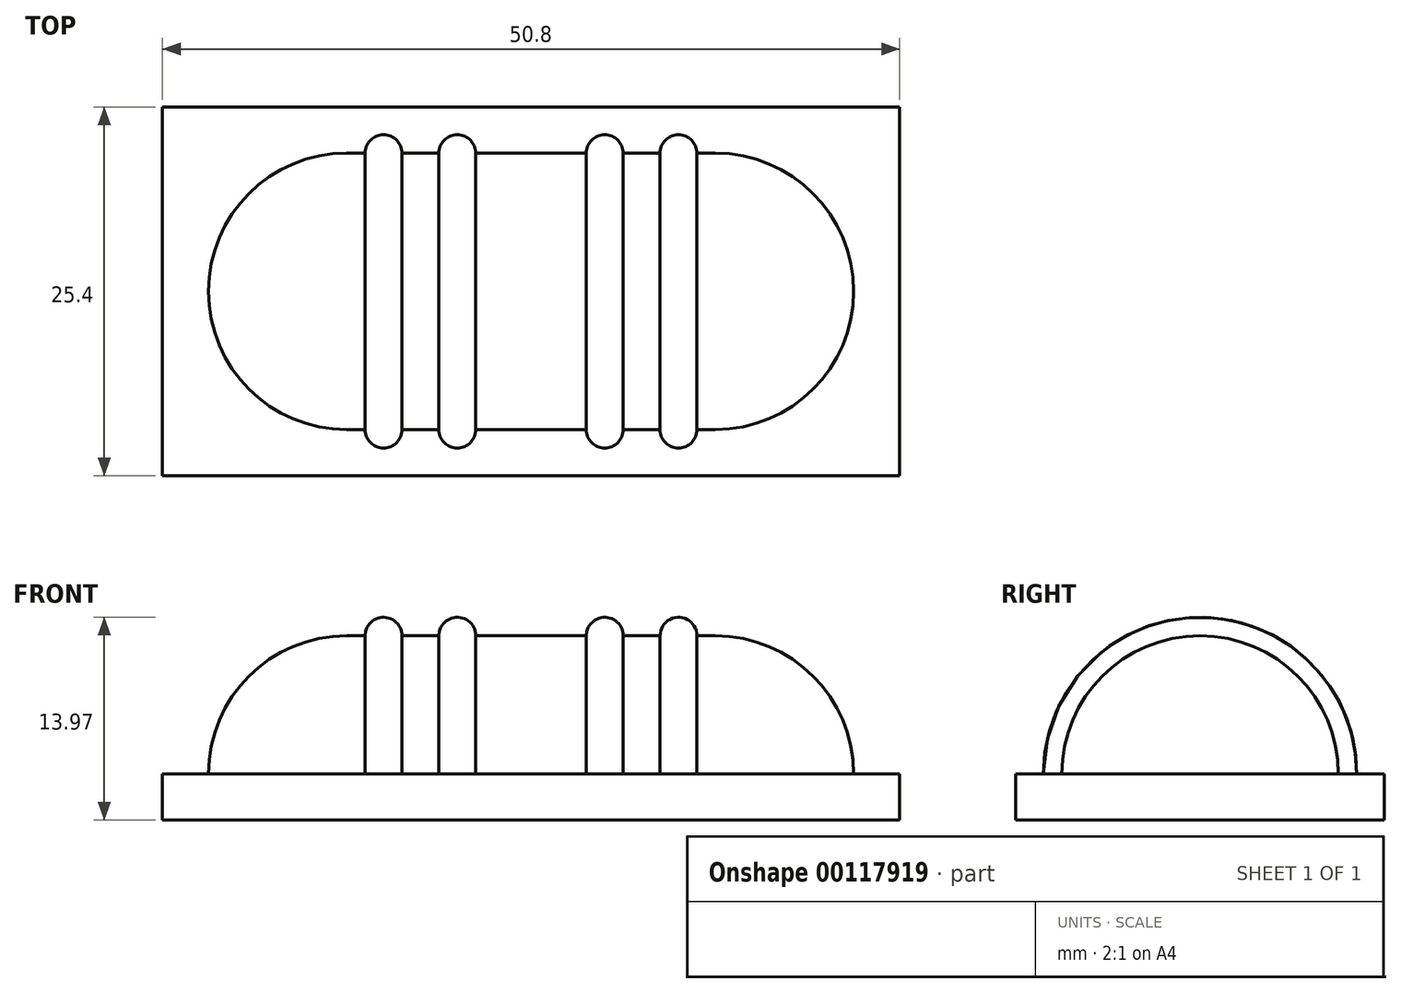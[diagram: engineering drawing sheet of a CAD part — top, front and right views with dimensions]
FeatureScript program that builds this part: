
annotation { "Feature Type Name" : "Feature", "Feature Type Description" : "" }
export const myFeature = defineFeature(function(context is Context, id is Id, definition is map)
    precondition{}
    {
        {
            var Q0;
            Q0=qCreatedBy(makeId("Top.planeOp"),FACE);
            var sketch = newSketch(context, id + "F0", { "sketchPlane" : qUnion([Q0])});
            skLineSegment(sketch, "E0.bottom", {"start": v(0, 0) * mm, "end": v(50.8, 0) * mm});
            skLineSegment(sketch, "E0.top", {"start": v(0, 25.4) * mm, "end": v(50.8, 25.4) * mm});
            skLineSegment(sketch, "E0.left", {"start": v(0, 0) * mm, "end": v(0, 25.4) * mm});
            skLineSegment(sketch, "E0.right", {"start": v(50.8, 0) * mm, "end": v(50.8, 25.4) * mm});
            skLineSegment(sketch, "E1", {"start": v(25.4, 25.4) * mm, "end": v(25.4, 0) * mm, "construction": true});
            skLineSegment(sketch, "E2.bottom", {"start": v(12.7, 22.22) * mm, "end": v(38.1, 22.22) * mm});
            skLineSegment(sketch, "E2.top", {"start": v(12.7, 3.18) * mm, "end": v(38.1, 3.18) * mm});
            skLineSegment(sketch, "E2.left", {"start": v(12.7, 22.22) * mm, "end": v(12.7, 3.18) * mm});
            skLineSegment(sketch, "E2.right", {"start": v(38.1, 22.22) * mm, "end": v(38.1, 3.18) * mm});
            skSolve(sketch);
        }
        {
            var Q0;
            Q0 = qSketchRegion(id + "F0", true);
            var Q1;
            Q1=makeQuery(id+"F0.imprint","IMPRINT",FACE,{"disambiguationData":[TD([[makeQuery(id+"F0.imprint","IMPRINT",EDGE,{"derivedFrom":sQuery(id+"F0.wireOp",EDGE,"E2.bottom")}),-1.0]])]});
            extrude(context, id + "F1", {"entities" : qUnion([Q0, Q1]), "depth" : 3.17 * mm});
        }
        {
            var Q0;
            Q0=makeQuery(id+"F1.opExtrude","CAP_FACE",FACE,{"disambiguationData":[OSD([sQuery(id+"F0.wireOp",EDGE,"E0.bottom"),sQuery(id+"F0.wireOp",EDGE,"E0.top"),sQuery(id+"F0.wireOp",EDGE,"E0.left"),sQuery(id+"F0.wireOp",EDGE,"E0.right")])],"isStart":false});
            var sketch = newSketch(context, id + "F2", { "sketchPlane" : qUnion([Q0])});
            skLineSegment(sketch, "E3.0", {"start": v(12.7, 22.22) * mm, "end": v(38.1, 22.22) * mm});
            skLineSegment(sketch, "E3.1", {"start": v(12.7, 22.22) * mm, "end": v(12.7, 3.18) * mm});
            skLineSegment(sketch, "E3.2", {"start": v(12.7, 3.18) * mm, "end": v(38.1, 3.18) * mm});
            skLineSegment(sketch, "E3.3", {"start": v(38.1, 22.22) * mm, "end": v(38.1, 3.18) * mm});
            skLineSegment(sketch, "E3.4", {"start": v(25.4, 25.4) * mm, "end": v(25.4, 0) * mm});
            skLineSegment(sketch, "E4", {"start": v(0, 12.7) * mm, "end": v(50.8, 12.7) * mm});
            skSolve(sketch);
        }
        {
            var Q0;
            {var subQ5=sQuery(id+"F2.wireOp",EDGE,"E3.3");Q0=makeQuery(id+"F2.imprint","IMPRINT",FACE,{"disambiguationData":[TD([[makeQuery(id+"F2.imprint","IMPRINT",EDGE,{"derivedFrom":subQ5}),1.0]])]});}
            var sketch = newSketch(context, id + "F3", { "sketchPlane" : qUnion([Q0])});
            skLineSegment(sketch, "E5.0", {"start": v(38.1, 22.22) * mm, "end": v(38.1, 3.18) * mm});
            skArc(sketch, "E6", {"start": v(38.1, 22.22) * mm, "mid": v(47.62, 12.7) * mm, "end": v(38.1, 3.18) * mm});
            skLineSegment(sketch, "E7.0", {"start": v(12.7, 22.22) * mm, "end": v(12.7, 3.18) * mm});
            skArc(sketch, "E8", {"start": v(12.7, 22.22) * mm, "mid": v(3.18, 12.7) * mm, "end": v(12.7, 3.18) * mm});
            skSolve(sketch);
        }
        {
            var Q0;
            {var subQ0=sQuery(id+"F2.wireOp",EDGE,"E3.2");var subQ1=sQuery(id+"F2.wireOp",EDGE,"E3.1");var subQ2=makeQuery(id+"F2.imprint","INTERSECT",VERTEX,{"derivedFrom":[subQ1,subQ0]});Q0=makeQuery(id+"F2.imprint","IMPRINT",FACE,{"disambiguationData":[TD([[makeQuery(id+"F2.imprint","IMPRINT",EDGE,{"disambiguationData":[TD([[subQ2,1.0]])],"derivedFrom":subQ1}),1.0]])]});}
            var Q1;
            {var subQ0=sQuery(id+"F2.wireOp",EDGE,"E3.3");var subQ1=sQuery(id+"F2.wireOp",EDGE,"E3.2");var subQ2=makeQuery(id+"F2.imprint","INTERSECT",VERTEX,{"derivedFrom":[subQ1,subQ0]});Q1=makeQuery(id+"F2.imprint","IMPRINT",FACE,{"disambiguationData":[TD([[makeQuery(id+"F2.imprint","IMPRINT",EDGE,{"disambiguationData":[TD([[subQ2,1.0]])],"derivedFrom":subQ1}),1.0]])]});}
            var Q2;
            Q2=sQuery(id+"F2.wireOp",EDGE,"E4");
            revolve(context, id + "F4", {"operationType" : NewBodyOperationType.ADD, "entities" : qUnion([Q0, Q1]), "axis" : qUnion([Q2]), "revolveType" : RevolveType.ONE_DIRECTION, "oppositeDirection" : true, "angle" : 180 * degree});
        }
        {
            var Q0;
            Q0=qCreatedBy(makeId("Front.planeOp"),FACE);
            var sketch = newSketch(context, id + "F5", { "sketchPlane" : qUnion([Q0])});
            skLineSegment(sketch, "E9.0", {"start": v(12.7, 12.7) * mm, "end": v(12.7, 3.17) * mm});
            skLineSegment(sketch, "E9.1", {"start": v(3.18, 3.18) * mm, "end": v(12.7, 3.18) * mm});
            skLineSegment(sketch, "E9.2", {"start": v(38.1, 12.7) * mm, "end": v(38.1, 3.18) * mm});
            skLineSegment(sketch, "E9.3", {"start": v(47.62, 3.18) * mm, "end": v(38.1, 3.18) * mm});
            skArc(sketch, "E10", {"start": v(12.7, 12.7) * mm, "mid": v(5.96, 9.91) * mm, "end": v(3.18, 3.18) * mm});
            skArc(sketch, "E11", {"start": v(38.1, 12.7) * mm, "mid": v(44.84, 9.91) * mm, "end": v(47.62, 3.18) * mm});
            skSolve(sketch);
        }
        {
            var Q0;
            {var subQ1=sQuery(id+"F3.wireOp",EDGE,"E5.0");var subQ5=sQuery(id+"F2.wireOp",EDGE,"E4");var subQ6=makeQuery(id+"F2.imprint","IMPRINT",EDGE,{"disambiguationData":[TD([[makeQuery(id+"F2.imprint","INTERSECT",VERTEX,{"derivedFrom":[makeQuery(id+"F1.opExtrude","CAP_EDGE",EDGE,{"disambiguationData":[OSD([sQuery(id+"F0.wireOp",EDGE,"E0.right")])],"isStart":false}),subQ5]}),1.0]])],"derivedFrom":subQ5});var subQ7=makeQuery(id+"F3.imprint","INTERSECT",VERTEX,{"derivedFrom":[subQ6,subQ1]});Q0=makeQuery(id+"F3.imprint","IMPRINT",FACE,{"disambiguationData":[TD([[makeQuery(id+"F3.imprint","IMPRINT",EDGE,{"disambiguationData":[TD([[subQ7,-1.0]])],"derivedFrom":subQ1}),1.0]])]});}
            var Q1;
            {var subQ1=sQuery(id+"F3.wireOp",EDGE,"E5.0");var subQ5=sQuery(id+"F2.wireOp",EDGE,"E4");var subQ6=makeQuery(id+"F2.imprint","IMPRINT",EDGE,{"disambiguationData":[TD([[makeQuery(id+"F2.imprint","INTERSECT",VERTEX,{"derivedFrom":[makeQuery(id+"F1.opExtrude","CAP_EDGE",EDGE,{"disambiguationData":[OSD([sQuery(id+"F0.wireOp",EDGE,"E0.right")])],"isStart":false}),subQ5]}),1.0]])],"derivedFrom":subQ5});var subQ7=makeQuery(id+"F3.imprint","INTERSECT",VERTEX,{"derivedFrom":[subQ6,subQ1]});Q1=makeQuery(id+"F3.imprint","IMPRINT",FACE,{"disambiguationData":[TD([[makeQuery(id+"F3.imprint","IMPRINT",EDGE,{"disambiguationData":[TD([[subQ7,1.0]])],"derivedFrom":subQ1}),1.0]])]});}
            var Q2;
            Q2=sQuery(id+"F5.wireOp",EDGE,"E11");
            sweep(context, id + "F6", {"operationType" : NewBodyOperationType.ADD, "profiles" : qUnion([Q0, Q1]), "path" : qUnion([Q2])});
        }
        {
            var Q0;
            Q0=makeQuery(id+"F3.imprint","IMPRINT",FACE,{"disambiguationData":[TD([[makeQuery(id+"F3.imprint","IMPRINT",EDGE,{"derivedFrom":sQuery(id+"F3.wireOp",EDGE,"E7.0")}),-1.0]])]});
            var Q1;
            Q1=sQuery(id+"F5.wireOp",EDGE,"E10");
            sweep(context, id + "F7", {"operationType" : NewBodyOperationType.ADD, "profiles" : qUnion([Q0]), "path" : qUnion([Q1])});
        }
        {
            var Q0;
            Q0=makeQuery(id+"F1.opExtrude","CAP_FACE",FACE,{"disambiguationData":[OSD([sQuery(id+"F0.wireOp",EDGE,"E0.bottom"),sQuery(id+"F0.wireOp",EDGE,"E0.top"),sQuery(id+"F0.wireOp",EDGE,"E0.left"),sQuery(id+"F0.wireOp",EDGE,"E0.right")])],"isStart":false});
            var sketch = newSketch(context, id + "F8", { "sketchPlane" : qUnion([Q0])});
            skLineSegment(sketch, "E12.0", {"start": v(25.4, 25.4) * mm, "end": v(25.4, 0) * mm, "construction": true});
            skLineSegment(sketch, "E13.0", {"start": v(12.7, 22.22) * mm, "end": v(38.1, 22.22) * mm});
            skLineSegment(sketch, "E13.1", {"start": v(12.7, 22.22) * mm, "end": v(12.7, 3.18) * mm});
            skLineSegment(sketch, "E13.2", {"start": v(38.1, 22.22) * mm, "end": v(38.1, 3.18) * mm});
            skLineSegment(sketch, "E13.3", {"start": v(12.7, 3.18) * mm, "end": v(38.1, 3.18) * mm});
            skArc(sketch, "E14", {"start": v(26.67, 3.17) * mm, "mid": v(25.4, 1.9) * mm, "end": v(24.13, 3.18) * mm});
            skArc(sketch, "E15.MirrorCS", {"start": v(24.13, 3.17) * mm, "mid": v(25.4, 1.9) * mm, "end": v(26.67, 3.18) * mm});
            skArc(sketch, "E16.1.0.0", {"start": v(29.21, 3.17) * mm, "mid": v(30.48, 1.9) * mm, "end": v(31.75, 3.18) * mm});
            skLineSegment(sketch, "E16.direction1", {"start": v(24.13, 3.17) * mm, "end": v(29.2, 3.17) * mm, "construction": true});
            skArc(sketch, "E17.1.0.0", {"start": v(19.05, 3.17) * mm, "mid": v(20.32, 1.9) * mm, "end": v(21.59, 3.18) * mm});
            skLineSegment(sketch, "E17.direction1", {"start": v(24.13, 3.17) * mm, "end": v(19.05, 3.17) * mm, "construction": true});
            skArc(sketch, "E18.0.2.0", {"start": v(34.3, 3.17) * mm, "mid": v(35.56, 1.9) * mm, "end": v(36.83, 3.18) * mm});
            skArc(sketch, "E19.0.2.0", {"start": v(13.97, 3.17) * mm, "mid": v(15.24, 1.9) * mm, "end": v(16.5, 3.18) * mm});
            skSolve(sketch);
        }
        {
            var Q0;
            {var subQ0=sQuery(id+"F8.wireOp",EDGE,"E17.1.0.0");Q0=makeQuery(id+"F8.imprint","IMPRINT",FACE,{"disambiguationData":[TD([[makeQuery(id+"F8.imprint","IMPRINT",EDGE,{"derivedFrom":subQ0}),1.0]])]});}
            var Q1;
            {var subQ0=sQuery(id+"F8.wireOp",EDGE,"E15.MirrorCS");Q1=makeQuery(id+"F8.imprint","IMPRINT",FACE,{"disambiguationData":[TD([[makeQuery(id+"F8.imprint","IMPRINT",EDGE,{"derivedFrom":subQ0}),1.0]])]});}
            var Q2;
            {var subQ0=sQuery(id+"F8.wireOp",EDGE,"E16.1.0.0");Q2=makeQuery(id+"F8.imprint","IMPRINT",FACE,{"disambiguationData":[TD([[makeQuery(id+"F8.imprint","IMPRINT",EDGE,{"derivedFrom":subQ0}),1.0]])]});}
            var Q3;
            {var subQ0=sQuery(id+"F8.wireOp",EDGE,"E19.0.2.0");Q3=makeQuery(id+"F8.imprint","IMPRINT",FACE,{"disambiguationData":[TD([[makeQuery(id+"F8.imprint","IMPRINT",EDGE,{"derivedFrom":subQ0}),1.0]])]});}
            var Q4;
            {var subQ0=sQuery(id+"F8.wireOp",EDGE,"E18.0.2.0");Q4=makeQuery(id+"F8.imprint","IMPRINT",FACE,{"disambiguationData":[TD([[makeQuery(id+"F8.imprint","IMPRINT",EDGE,{"derivedFrom":subQ0}),1.0]])]});}
            var Q5;
            Q5=makeQuery(id+"F6.boolean.opBoolean","MERGE",EDGE,{"derivedFrom":[makeQuery(id+"F4.opRevolve","SWEPT_EDGE",EDGE,{"disambiguationData":[OSD([sQuery(id+"F2.wireOp",EDGE,"E3.2"),sQuery(id+"F2.wireOp",EDGE,"E3.3")])]}),makeQuery(id+"F6.opSweep","CAP_EDGE",EDGE,{"disambiguationData":[OSD([sQuery(id+"F3.wireOp",EDGE,"E6"),sQuery(id+"F5.wireOp",VERTEX,"E11.start")])],"isStart":false})]});
            sweep(context, id + "F9", {"operationType" : NewBodyOperationType.ADD, "profiles" : qUnion([Q0, Q1, Q2, Q3, Q4]), "path" : qUnion([Q5])});
        }
    });
